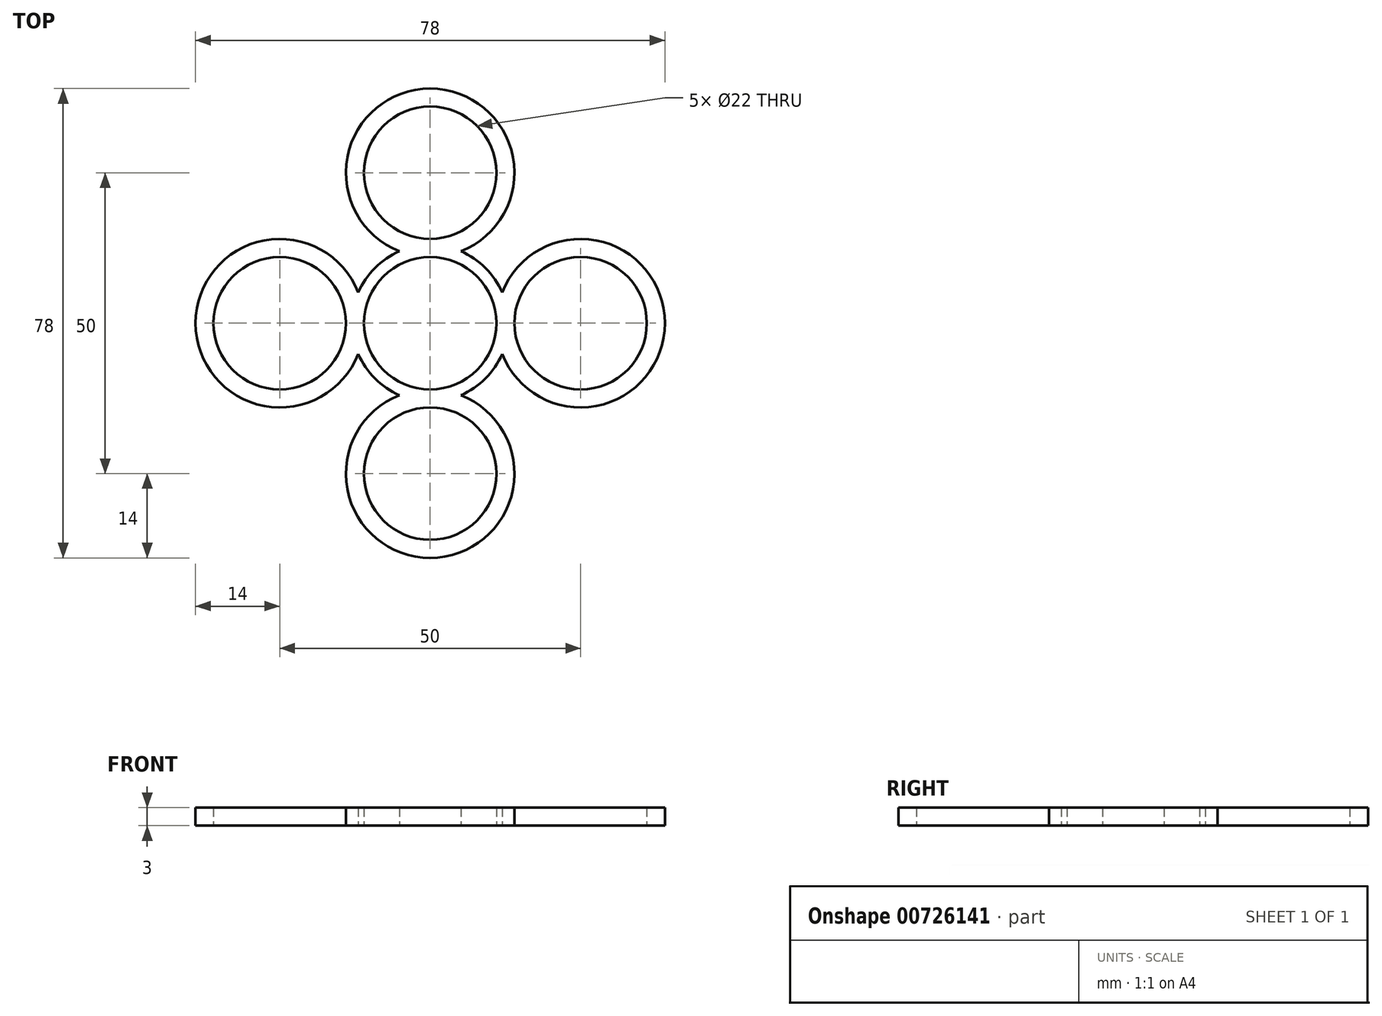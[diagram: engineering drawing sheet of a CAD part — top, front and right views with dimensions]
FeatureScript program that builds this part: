
annotation { "Feature Type Name" : "Feature", "Feature Type Description" : "" }
export const myFeature = defineFeature(function(context is Context, id is Id, definition is map)
    precondition{}
    {
        {
            var Q0;
            Q0=qCreatedBy(makeId("Top.planeOp"),FACE);
            var sketch = newSketch(context, id + "F0", { "sketchPlane" : qUnion([Q0])});
            skArc(sketch, "E0", {"start": v(7.78, 7.78) * mm, "mid": v(0, 11) * mm, "end": v(-7.78, 7.78) * mm});
            skArc(sketch, "E1", {"start": v(-5.1, 11.96) * mm, "mid": v(-7.28, 10.77) * mm, "end": v(-9.2, 9.2) * mm});
            skCircle(sketch, "E2", {"center": v(0, 25) * mm, "radius": 11 * mm});
            skArc(sketch, "E3", {"start": v(5.1, 11.96) * mm, "mid": v(0, 39) * mm, "end": v(-5.1, 11.96) * mm});
            skArc(sketch, "E4.trimOffspring", {"start": v(9.2, 9.2) * mm, "mid": v(7.28, 10.77) * mm, "end": v(5.1, 11.96) * mm});
            skArc(sketch, "E5.1.0", {"start": v(-11.96, 5.1) * mm, "mid": v(-39, 0) * mm, "end": v(-11.96, -5.1) * mm});
            skCircle(sketch, "E5.1.1", {"center": v(-25, 0) * mm, "radius": 11 * mm});
            skArc(sketch, "E5.1.2", {"start": v(-11.96, -5.1) * mm, "mid": v(-10.77, -7.28) * mm, "end": v(-9.2, -9.2) * mm});
            skArc(sketch, "E5.1.3", {"start": v(-9.2, 9.2) * mm, "mid": v(-10.77, 7.28) * mm, "end": v(-11.96, 5.1) * mm});
            skArc(sketch, "E5.1.4", {"start": v(-7.78, 7.78) * mm, "mid": v(-11, 0) * mm, "end": v(-7.78, -7.78) * mm});
            skArc(sketch, "E5.2.0", {"start": v(-5.1, -11.96) * mm, "mid": v(0, -39) * mm, "end": v(5.1, -11.96) * mm});
            skCircle(sketch, "E5.2.1", {"center": v(0, -25) * mm, "radius": 11 * mm});
            skArc(sketch, "E5.2.2", {"start": v(5.1, -11.96) * mm, "mid": v(7.28, -10.77) * mm, "end": v(9.2, -9.2) * mm});
            skArc(sketch, "E5.2.3", {"start": v(-9.2, -9.2) * mm, "mid": v(-7.28, -10.77) * mm, "end": v(-5.1, -11.96) * mm});
            skArc(sketch, "E5.2.4", {"start": v(-7.78, -7.78) * mm, "mid": v(0, -11) * mm, "end": v(7.78, -7.78) * mm});
            skArc(sketch, "E5.3.0", {"start": v(11.96, -5.1) * mm, "mid": v(39, 0) * mm, "end": v(11.96, 5.1) * mm});
            skCircle(sketch, "E5.3.1", {"center": v(25, 0) * mm, "radius": 11 * mm});
            skArc(sketch, "E5.3.2", {"start": v(11.96, 5.1) * mm, "mid": v(10.77, 7.28) * mm, "end": v(9.2, 9.2) * mm});
            skArc(sketch, "E5.3.3", {"start": v(9.2, -9.2) * mm, "mid": v(10.77, -7.28) * mm, "end": v(11.96, -5.1) * mm});
            skArc(sketch, "E5.3.4", {"start": v(7.78, -7.78) * mm, "mid": v(11, 0) * mm, "end": v(7.78, 7.78) * mm});
            skSolve(sketch);
        }
        {
            var Q0;
            Q0 = qSketchRegion(id + "F0", true);
            extrude(context, id + "F1", {"entities" : qUnion([Q0]), "depth" : 3 * mm, "offsetDistance" : 25 * mm});
        }
    });
